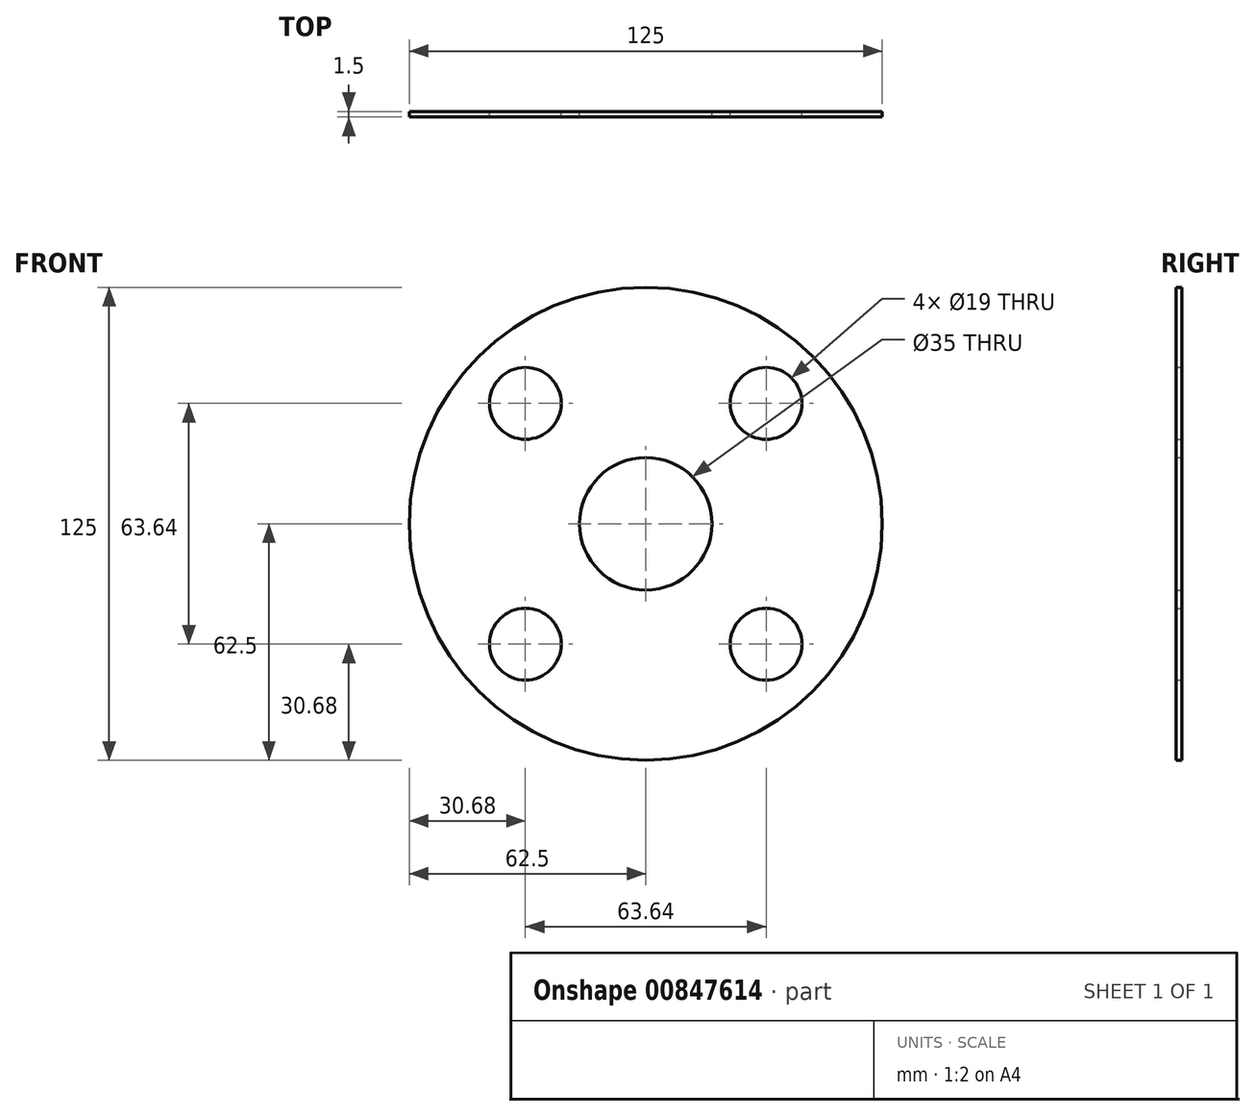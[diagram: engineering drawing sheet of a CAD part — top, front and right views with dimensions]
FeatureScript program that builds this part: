
annotation { "Feature Type Name" : "Feature", "Feature Type Description" : "" }
export const myFeature = defineFeature(function(context is Context, id is Id, definition is map)
    precondition{}
    {
        {
            var Q0;
            Q0=qCreatedBy(makeId("Front.planeOp"),FACE);
            var sketch = newSketch(context, id + "F0", { "sketchPlane" : qUnion([Q0])});
            skCircle(sketch, "E0", {"center": v(0, 0) * mm, "radius": 62.5 * mm});
            skCircle(sketch, "E1", {"center": v(0, 0) * mm, "radius": 17.5 * mm});
            skLineSegment(sketch, "E2", {"start": v(-83.51, 0) * mm, "end": v(92.26, 0) * mm, "construction": true});
            skLineSegment(sketch, "E3", {"start": v(58.75, 58.75) * mm, "end": v(-63.77, -63.77) * mm, "construction": true});
            skCircle(sketch, "E4", {"center": v(0, 0) * mm, "radius": 45 * mm, "construction": true});
            skCircle(sketch, "E5", {"center": v(31.82, 31.82) * mm, "radius": 9.5 * mm});
            skCircle(sketch, "E6.1.0", {"center": v(-31.82, 31.82) * mm, "radius": 9.5 * mm});
            skCircle(sketch, "E6.2.0", {"center": v(-31.82, -31.82) * mm, "radius": 9.5 * mm});
            skCircle(sketch, "E6.3.0", {"center": v(31.82, -31.82) * mm, "radius": 9.5 * mm});
            skSolve(sketch);
        }
        {
            var Q0;
            Q0 = qSketchRegion(id + "F0", true);
            extrude(context, id + "F1", {"entities" : qUnion([Q0]), "depth" : 1.5 * mm, "offsetDistance" : 25 * mm});
        }
    });
